# Revit family: Maxlogic Conventional Fire Alarm Panels small
name_source: partatom
category: Fire Alarm Devices
units: mm (PartAtom-declared; Revit-internal decimal feet)

## family parameters
Cut with Voids When Loaded = No
Host = Face
Maintain Annotation Orientation = Yes
OmniClass Number = 23.85.30.21
OmniClass Title = Environmental Detection/Registration
Part Type = Normal
Room Calculation Point = No
Round Connector Dimension = Use Diameter
Shared = No

## types (3) — shared parameters
Battery = 2 X (12V DC 2,1 Ah )
Code Performance = EN 54-2 / EN 54-4
Color = White
External supply = 220 V AC
Fax Number = (+)90 216 466 45 10
Installation Manual = https://mavilielektronik.com
Main Material = Metal Grey
Manufacturer = Mavili Elektronik Ticaret A.Ş.
Model = Maxlogic
Mounting surface = Wall mount
Nominal Depth = 90 mm
Nominal Height = 240 mm
Nominal Wıdth = 320 mm
Operating temperature = (-5°C) - (+40°C)
Protection Sign = IP 30
Secondary Material = White Plastic ABS
URL = https://www.mavili.com.tr
Warranty Duration Labor = 2
Warranty Duration Parts = 2
Warranty Duration Unit = Year
Weight = 3450 gr
zero-valued in all types: Cost, Default Elevation

## per-type parameters (varying)
| type | 2 led | 4 led | Description | Product Code |
| Maxlogic Conventional Fire Alarm Panel, 2 Zone | No | No | Conventional Fire Alarm Panel, 2 Zone | ML-2222 |
| Maxlogic Conventional Fire Alarm Panel, 4 Zone | Yes | No | Conventional Fire Alarm Panel, 4 Zone | ML-2224 |
| Maxlogic Conventional Fire Alarm Panel, 8 Zone | Yes | Yes | Conventional Fire Alarm Panel, 8 Zone | ML-2228 |

## geometry (parser evidence)
native form markers: Sweep x2
no freeform markers — native parametric forms only
